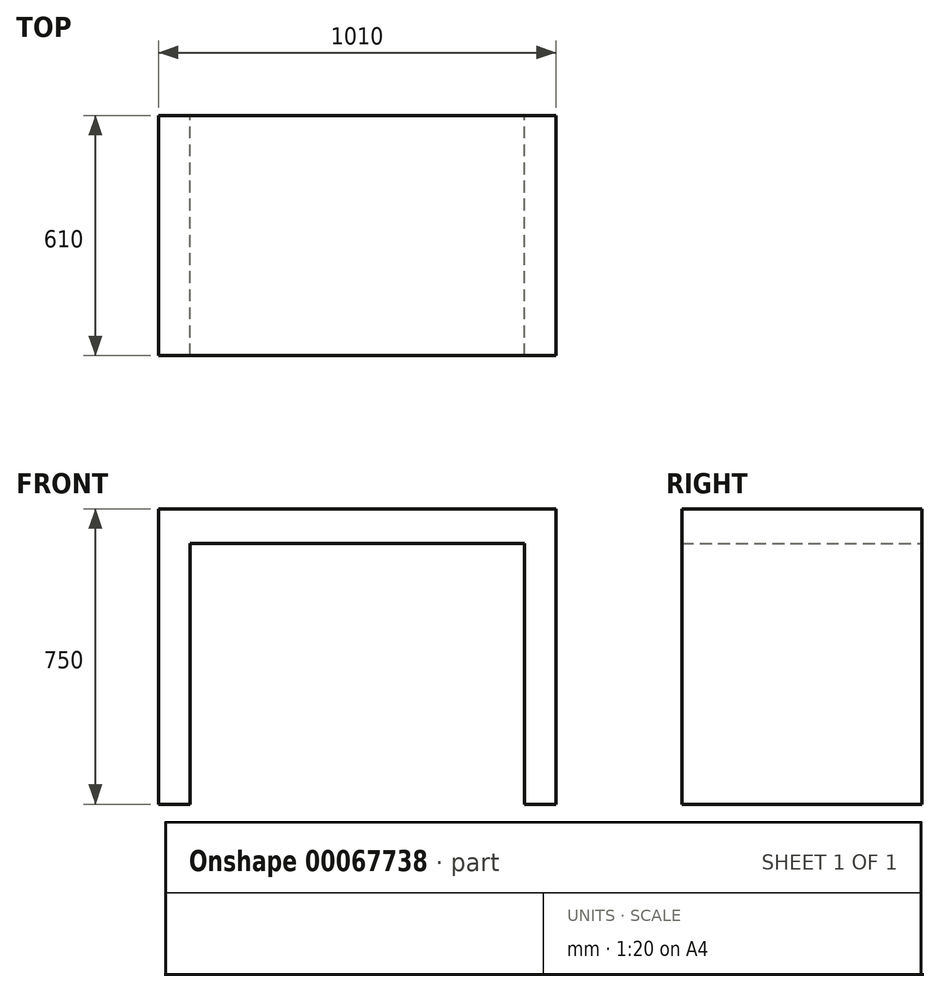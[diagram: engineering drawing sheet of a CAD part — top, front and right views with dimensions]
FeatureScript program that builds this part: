
annotation { "Feature Type Name" : "Feature", "Feature Type Description" : "" }
export const myFeature = defineFeature(function(context is Context, id is Id, definition is map)
    precondition{}
    {
        {
            var Q0;
            Q0=qCreatedBy(makeId("Front.planeOp"),FACE);
            var sketch = newSketch(context, id + "F0", { "sketchPlane" : qUnion([Q0])});
            skLineSegment(sketch, "E0", {"start": v(0, 0) * mm, "end": v(0, 750) * mm});
            skLineSegment(sketch, "E1", {"start": v(0, 750) * mm, "end": v(1010, 750) * mm});
            skLineSegment(sketch, "E2", {"start": v(1010, 750) * mm, "end": v(1010, 0) * mm});
            skLineSegment(sketch, "E3", {"start": v(1010, 0) * mm, "end": v(930, 0) * mm});
            skLineSegment(sketch, "E4", {"start": v(930, 0) * mm, "end": v(930, 662.2) * mm});
            skLineSegment(sketch, "E5", {"start": v(930, 662.2) * mm, "end": v(80, 662.2) * mm});
            skLineSegment(sketch, "E6", {"start": v(80, 662.2) * mm, "end": v(80, 0) * mm});
            skLineSegment(sketch, "E7", {"start": v(80, 0) * mm, "end": v(0, 0) * mm});
            skSolve(sketch);
        }
        {
            var Q0;
            Q0=makeQuery(id+"F0.imprint","IMPRINT",FACE,{"disambiguationData":[TD([[makeQuery(id+"F0.imprint","IMPRINT",EDGE,{"derivedFrom":sQuery(id+"F0.wireOp",EDGE,"E0")}),-1.0]])]});
            extrude(context, id + "F1", {"entities" : qUnion([Q0]), "depth" : 610 * mm});
        }
    });
